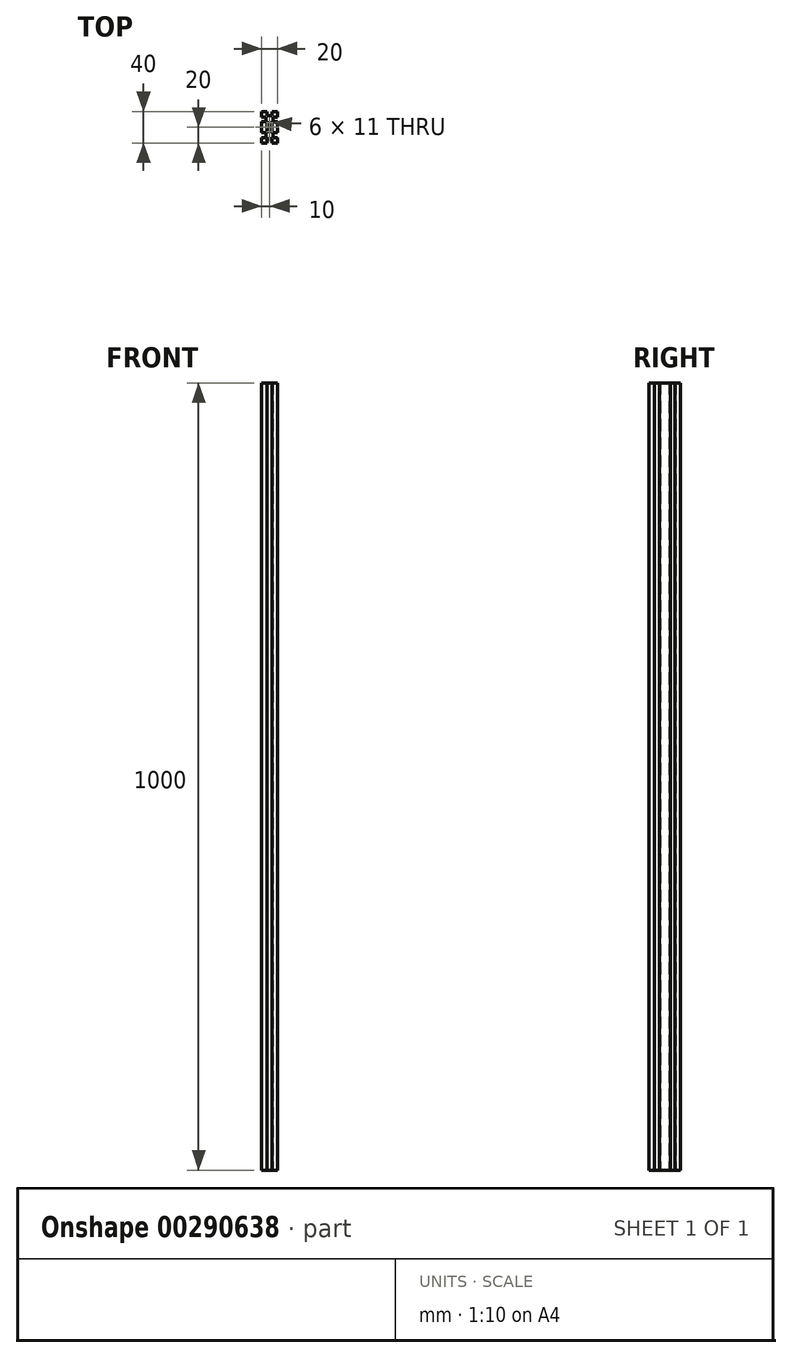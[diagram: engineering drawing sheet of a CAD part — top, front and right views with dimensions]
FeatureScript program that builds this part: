
annotation { "Feature Type Name" : "Feature", "Feature Type Description" : "" }
export const myFeature = defineFeature(function(context is Context, id is Id, definition is map)
    precondition{}
    {
        {
            var Q0;
            Q0=qCreatedBy(makeId("Top.planeOp"),FACE);
            var sketch = newSketch(context, id + "F0", { "sketchPlane" : qUnion([Q0])});
            skLineSegment(sketch, "E0.bottom", {"start": v(0, 0) * mm, "end": v(7, 0) * mm});
            skLineSegment(sketch, "E0.top", {"start": v(0, 20) * mm, "end": v(20, 20) * mm});
            skLineSegment(sketch, "E0.left", {"start": v(0, 0) * mm, "end": v(0, 20) * mm});
            skLineSegment(sketch, "E0.right", {"start": v(20, 0) * mm, "end": v(20, 20) * mm});
            skLineSegment(sketch, "E1.bottom", {"start": v(7, 20) * mm, "end": v(13, 20) * mm});
            skLineSegment(sketch, "E1.top", {"start": v(7, 14.5) * mm, "end": v(13, 14.5) * mm});
            skLineSegment(sketch, "E1.left", {"start": v(7, 20) * mm, "end": v(7, 14.5) * mm});
            skLineSegment(sketch, "E1.right", {"start": v(13, 20) * mm, "end": v(13, 14.5) * mm});
            skLineSegment(sketch, "E2.bottom", {"start": v(20, 13) * mm, "end": v(14.5, 13) * mm});
            skLineSegment(sketch, "E2.top", {"start": v(20, 7) * mm, "end": v(14.5, 7) * mm});
            skLineSegment(sketch, "E2.left", {"start": v(20, 13) * mm, "end": v(20, 7) * mm});
            skLineSegment(sketch, "E2.right", {"start": v(14.5, 13) * mm, "end": v(14.5, 7) * mm});
            skLineSegment(sketch, "E3.top", {"start": v(13, 5.5) * mm, "end": v(7, 5.5) * mm});
            skLineSegment(sketch, "E3.left", {"start": v(13, 0) * mm, "end": v(13, 5.5) * mm});
            skLineSegment(sketch, "E3.right", {"start": v(7, 0) * mm, "end": v(7, 5.5) * mm});
            skLineSegment(sketch, "E4.bottom", {"start": v(0, 7) * mm, "end": v(5.5, 7) * mm});
            skLineSegment(sketch, "E4.top", {"start": v(0, 13) * mm, "end": v(5.5, 13) * mm});
            skLineSegment(sketch, "E4.left", {"start": v(0, 7) * mm, "end": v(0, 13) * mm});
            skLineSegment(sketch, "E4.right", {"start": v(5.5, 7) * mm, "end": v(5.5, 13) * mm});
            skLineSegment(sketch, "E5.MirrorCS", {"start": v(5.5, -7) * mm, "end": v(5.5, -13) * mm});
            skLineSegment(sketch, "E6.MirrorCS", {"start": v(13, -5.5) * mm, "end": v(7, -5.5) * mm});
            skLineSegment(sketch, "E7.MirrorCS", {"start": v(0, -20) * mm, "end": v(20, -20) * mm});
            skLineSegment(sketch, "E8.MirrorCS", {"start": v(7, -20) * mm, "end": v(13, -20) * mm});
            skLineSegment(sketch, "E9.MirrorCS", {"start": v(7, -14.5) * mm, "end": v(13, -14.5) * mm});
            skLineSegment(sketch, "E10.MirrorCS", {"start": v(7, -20) * mm, "end": v(7, -14.5) * mm});
            skLineSegment(sketch, "E11.MirrorCS", {"start": v(13, -20) * mm, "end": v(13, -14.5) * mm});
            skLineSegment(sketch, "E12.MirrorCS", {"start": v(20, -13) * mm, "end": v(14.5, -13) * mm});
            skLineSegment(sketch, "E13.MirrorCS", {"start": v(20, -7) * mm, "end": v(14.5, -7) * mm});
            skLineSegment(sketch, "E14.MirrorCS", {"start": v(20, -13) * mm, "end": v(20, -7) * mm});
            skLineSegment(sketch, "E15.MirrorCS", {"start": v(14.5, -13) * mm, "end": v(14.5, -7) * mm});
            skLineSegment(sketch, "E16.MirrorCS", {"start": v(0, -7) * mm, "end": v(5.5, -7) * mm});
            skLineSegment(sketch, "E17.MirrorCS", {"start": v(0, -13) * mm, "end": v(5.5, -13) * mm});
            skLineSegment(sketch, "E18.MirrorCS", {"start": v(0, -7) * mm, "end": v(0, -13) * mm});
            skLineSegment(sketch, "E19.MirrorCS", {"start": v(7, 0) * mm, "end": v(7, -5.5) * mm});
            skLineSegment(sketch, "E20.MirrorCS", {"start": v(20, 0) * mm, "end": v(20, -20) * mm});
            skLineSegment(sketch, "E21.MirrorCS", {"start": v(0, 0) * mm, "end": v(0, -20) * mm});
            skLineSegment(sketch, "E22.MirrorCS", {"start": v(13, 0) * mm, "end": v(13, -5.5) * mm});
            skLineSegment(sketch, "E23.trimOffspring", {"start": v(13, 0) * mm, "end": v(20, 0) * mm});
            skSolve(sketch);
        }
        {
            var Q0;
            Q0=makeQuery(id+"F0.imprint","IMPRINT",FACE,{"disambiguationData":[TD([[makeQuery(id+"F0.imprint","IMPRINT",EDGE,{"derivedFrom":sQuery(id+"F0.wireOp",EDGE,"E1.top")}),-1.0]])]});
            var Q1;
            {var subQ8=sQuery(id+"F0.wireOp",EDGE,"E0.bottom");Q1=makeQuery(id+"F0.imprint","IMPRINT",FACE,{"disambiguationData":[TD([[makeQuery(id+"F0.imprint","IMPRINT",EDGE,{"derivedFrom":subQ8}),-1.0]])]});}
            extrude(context, id + "F1", {"entities" : qUnion([Q0, Q1]), "depth" : 1000 * mm});
        }
    });
